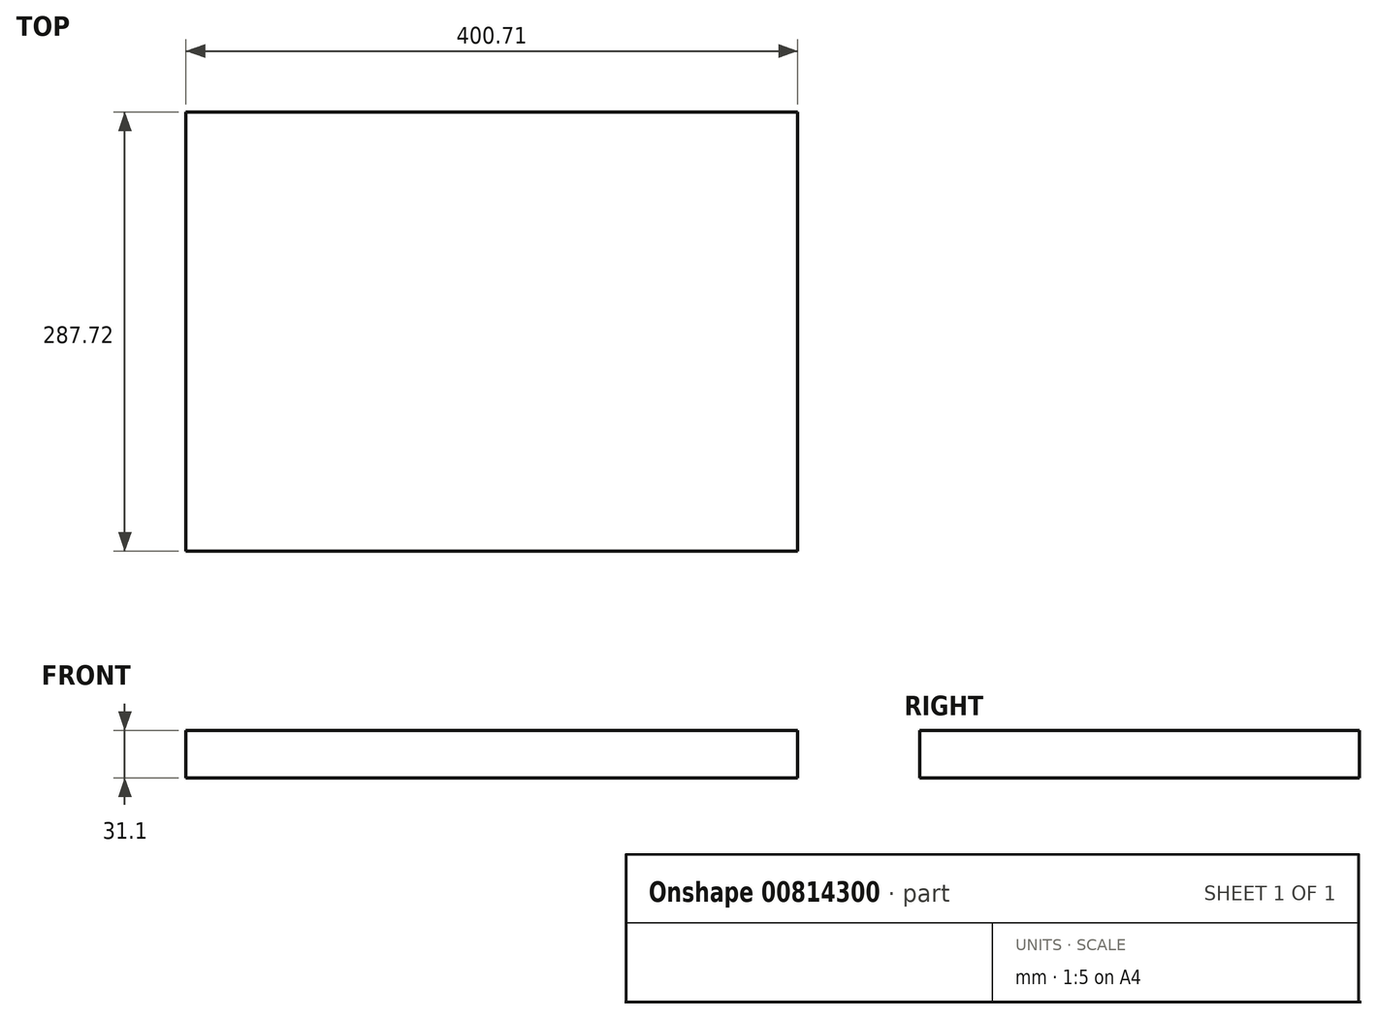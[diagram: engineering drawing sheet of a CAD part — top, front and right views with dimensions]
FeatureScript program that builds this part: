
annotation { "Feature Type Name" : "Feature", "Feature Type Description" : "" }
export const myFeature = defineFeature(function(context is Context, id is Id, definition is map)
    precondition{}
    {
        {
            var Q0;
            Q0=qCreatedBy(makeId("Top.planeOp"),FACE);
            var sketch = newSketch(context, id + "F0", { "sketchPlane" : qUnion([Q0])});
            skLineSegment(sketch, "E0.bottom", {"start": v(-198.23, 143.83) * mm, "end": v(202.48, 143.83) * mm});
            skLineSegment(sketch, "E0.top", {"start": v(-198.23, -143.89) * mm, "end": v(202.48, -143.89) * mm});
            skLineSegment(sketch, "E0.left", {"start": v(-198.23, 143.83) * mm, "end": v(-198.23, -143.89) * mm});
            skLineSegment(sketch, "E0.right", {"start": v(202.48, 143.83) * mm, "end": v(202.48, -143.89) * mm});
            skSolve(sketch);
        }
        {
            var Q0;
            Q0=makeQuery(id+"F0.imprint","IMPRINT",FACE,{"disambiguationData":[TD([[makeQuery(id+"F0.imprint","IMPRINT",EDGE,{"derivedFrom":sQuery(id+"F0.wireOp",EDGE,"E0.bottom")}),-1.0]])]});
            extrude(context, id + "F1", {"entities" : qUnion([Q0]), "oppositeDirection" : true, "depth" : 31.1 * mm, "offsetDistance" : 25.4 * mm});
        }
    });
